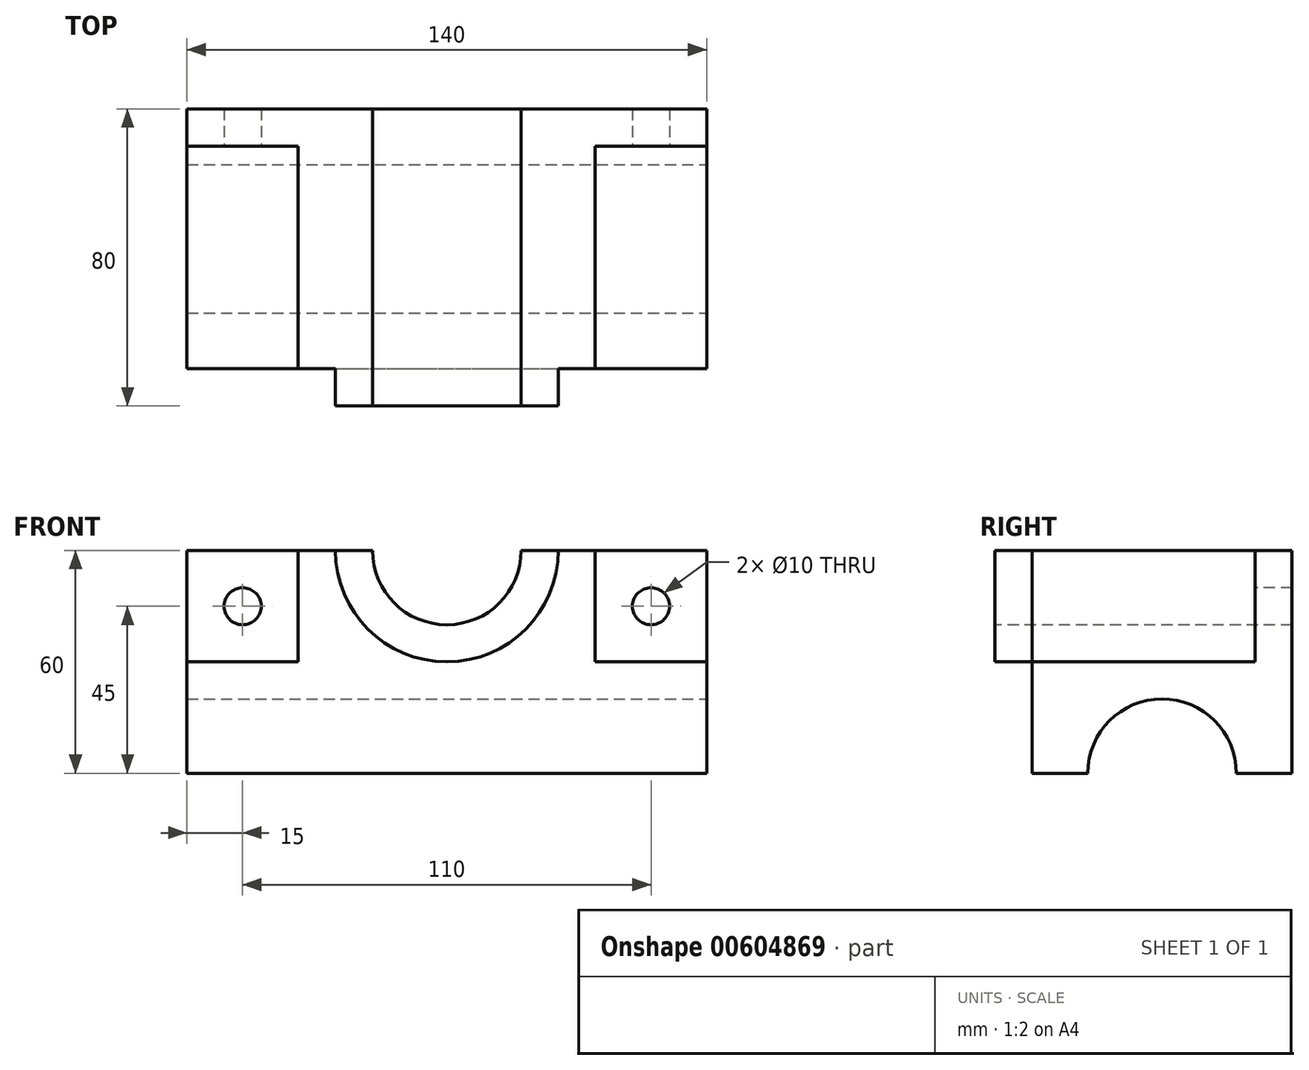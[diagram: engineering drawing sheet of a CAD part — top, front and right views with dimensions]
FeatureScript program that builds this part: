
annotation { "Feature Type Name" : "Feature", "Feature Type Description" : "" }
export const myFeature = defineFeature(function(context is Context, id is Id, definition is map)
    precondition{}
    {
        {
            var Q0;
            Q0=qCreatedBy(makeId("Top.planeOp"),FACE);
            var sketch = newSketch(context, id + "F0", { "sketchPlane" : qUnion([Q0])});
            skLineSegment(sketch, "E0.bottom", {"start": v(0, 0) * mm, "end": v(140, 0) * mm});
            skLineSegment(sketch, "E0.top", {"start": v(0, 70) * mm, "end": v(140, 70) * mm});
            skLineSegment(sketch, "E0.left", {"start": v(0, 0) * mm, "end": v(0, 70) * mm});
            skLineSegment(sketch, "E0.right", {"start": v(140, 0) * mm, "end": v(140, 70) * mm});
            skSolve(sketch);
        }
        {
            var Q0;
            Q0=makeQuery(id+"F0.imprint","IMPRINT",FACE,{"disambiguationData":[TD([[makeQuery(id+"F0.imprint","IMPRINT",EDGE,{"derivedFrom":sQuery(id+"F0.wireOp",EDGE,"E0.bottom")}),1.0]])]});
            extrude(context, id + "F1", {"entities" : qUnion([Q0]), "depth" : 60 * mm, "offsetDistance" : 25 * mm});
        }
        {
            var Q0;
            Q0=makeQuery(id+"F1.opExtrude","SWEPT_FACE",FACE,{"disambiguationData":[OSD([sQuery(id+"F0.wireOp",EDGE,"E0.bottom")])]});
            var sketch = newSketch(context, id + "F2", { "sketchPlane" : qUnion([Q0])});
            skLineSegment(sketch, "E1.bottom", {"start": v(140, 60) * mm, "end": v(110, 60) * mm});
            skLineSegment(sketch, "E1.top", {"start": v(140, 30) * mm, "end": v(110, 30) * mm});
            skLineSegment(sketch, "E1.left", {"start": v(140, 60) * mm, "end": v(140, 30) * mm});
            skLineSegment(sketch, "E1.right", {"start": v(110, 60) * mm, "end": v(110, 30) * mm});
            skLineSegment(sketch, "E2.bottom", {"start": v(0, 60) * mm, "end": v(30, 60) * mm});
            skLineSegment(sketch, "E2.top", {"start": v(0, 30) * mm, "end": v(30, 30) * mm});
            skLineSegment(sketch, "E2.left", {"start": v(0, 60) * mm, "end": v(0, 30) * mm});
            skLineSegment(sketch, "E2.right", {"start": v(30, 60) * mm, "end": v(30, 30) * mm});
            skSolve(sketch);
        }
        {
            var Q0;
            Q0=makeQuery(id+"F2.imprint","IMPRINT",FACE,{"disambiguationData":[TD([[makeQuery(id+"F2.imprint","IMPRINT",EDGE,{"derivedFrom":sQuery(id+"F2.wireOp",EDGE,"E2.bottom")}),-1.0]])]});
            extrude(context, id + "F3", {"entities" : qUnion([Q0]), "operationType" : NewBodyOperationType.REMOVE, "oppositeDirection" : true, "depth" : 60 * mm, "offsetDistance" : 25 * mm});
        }
        {
            var Q0;
            Q0=makeQuery(id+"F2.imprint","IMPRINT",FACE,{"disambiguationData":[TD([[makeQuery(id+"F2.imprint","IMPRINT",EDGE,{"derivedFrom":sQuery(id+"F2.wireOp",EDGE,"E1.bottom")}),-1.0]])]});
            extrude(context, id + "F4", {"entities" : qUnion([Q0]), "operationType" : NewBodyOperationType.REMOVE, "oppositeDirection" : true, "depth" : 60 * mm, "offsetDistance" : 25 * mm});
        }
        {
            var Q0;
            Q0=makeQuery(id+"F3.boolean.opBoolean","COPY",FACE,{"derivedFrom":makeQuery(id+"F3.opExtrude","CAP_FACE",FACE,{"disambiguationData":[OSD([sQuery(id+"F2.wireOp",EDGE,"E2.bottom"),sQuery(id+"F2.wireOp",EDGE,"E2.top"),sQuery(id+"F2.wireOp",EDGE,"E2.left"),sQuery(id+"F2.wireOp",EDGE,"E2.right")])],"isStart":false})});
            var sketch = newSketch(context, id + "F5", { "sketchPlane" : qUnion([Q0])});
            skLineSegment(sketch, "E3", {"start": v(15, 60) * mm, "end": v(15, 45) * mm, "construction": true});
            skLineSegment(sketch, "E4", {"start": v(0, 45) * mm, "end": v(15, 45) * mm, "construction": true});
            skCircle(sketch, "E5", {"center": v(15, 45) * mm, "radius": 5 * mm});
            skLineSegment(sketch, "E6", {"start": v(125, 60) * mm, "end": v(125, 45) * mm, "construction": true});
            skLineSegment(sketch, "E7", {"start": v(140, 45) * mm, "end": v(125, 45) * mm, "construction": true});
            skCircle(sketch, "E8", {"center": v(125, 45) * mm, "radius": 5 * mm});
            skSolve(sketch);
        }
        {
            var Q0;
            Q0=makeQuery(id+"F5.imprint","IMPRINT",FACE,{"disambiguationData":[TD([[makeQuery(id+"F5.imprint","IMPRINT",EDGE,{"derivedFrom":sQuery(id+"F5.wireOp",EDGE,"E5")}),1.0]])]});
            var Q1;
            Q1=makeQuery(id+"F5.imprint","IMPRINT",FACE,{"disambiguationData":[TD([[makeQuery(id+"F5.imprint","IMPRINT",EDGE,{"derivedFrom":sQuery(id+"F5.wireOp",EDGE,"E8")}),1.0]])]});
            extrude(context, id + "F6", {"entities" : qUnion([Q0, Q1]), "operationType" : NewBodyOperationType.REMOVE, "endBound" : BoundingType.UP_TO_NEXT, "oppositeDirection" : true, "depth" : 25 * mm, "offsetDistance" : 25 * mm});
        }
        {
            var Q0;
            Q0=makeQuery(id+"F1.opExtrude","SWEPT_FACE",FACE,{"disambiguationData":[OSD([sQuery(id+"F0.wireOp",EDGE,"E0.bottom")])]});
            var sketch = newSketch(context, id + "F7", { "sketchPlane" : qUnion([Q0])});
            skCircle(sketch, "E9", {"center": v(70, 60) * mm, "radius": 20 * mm});
            skCircle(sketch, "E10", {"center": v(70, 60) * mm, "radius": 30 * mm});
            skSolve(sketch);
        }
        {
            var Q0;
            {var subQ0=sQuery(id+"F7.wireOp",EDGE,"E9");var subQ1=makeQuery(id+"F1.opExtrude","CAP_EDGE",EDGE,{"disambiguationData":[OSD([sQuery(id+"F0.wireOp",EDGE,"E0.bottom")])],"isStart":false});var subQ2=makeQuery(id+"F7.imprint","INTERSECT",VERTEX,{"disambiguationData":[OD(0.0)],"derivedFrom":[subQ1,subQ0]});Q0=makeQuery(id+"F7.imprint","IMPRINT",FACE,{"disambiguationData":[TD([[makeQuery(id+"F7.imprint","IMPRINT",EDGE,{"disambiguationData":[TD([[subQ2,-1.0]])],"derivedFrom":subQ0}),1.0]])]});}
            extrude(context, id + "F8", {"entities" : qUnion([Q0]), "operationType" : NewBodyOperationType.REMOVE, "endBound" : BoundingType.UP_TO_NEXT, "oppositeDirection" : true, "depth" : 25 * mm, "offsetDistance" : 25 * mm});
        }
        {
            var Q0;
            Q0=makeQuery(id+"F1.opExtrude","SWEPT_FACE",FACE,{"disambiguationData":[OSD([sQuery(id+"F0.wireOp",EDGE,"E0.right")])]});
            var sketch = newSketch(context, id + "F9", { "sketchPlane" : qUnion([Q0])});
            skCircle(sketch, "E11", {"center": v(35, 0) * mm, "radius": 20 * mm});
            skSolve(sketch);
        }
        {
            var Q0;
            {var subQ0=sQuery(id+"F9.wireOp",EDGE,"E11");var subQ1=makeQuery(id+"F1.opExtrude","CAP_EDGE",EDGE,{"disambiguationData":[OSD([sQuery(id+"F0.wireOp",EDGE,"E0.right")])],"isStart":true});var subQ2=makeQuery(id+"F9.imprint","INTERSECT",VERTEX,{"disambiguationData":[OD(0.0)],"derivedFrom":[subQ1,subQ0]});Q0=makeQuery(id+"F9.imprint","IMPRINT",FACE,{"disambiguationData":[TD([[makeQuery(id+"F9.imprint","IMPRINT",EDGE,{"disambiguationData":[TD([[subQ2,1.0]])],"derivedFrom":subQ0}),1.0]])]});}
            extrude(context, id + "F10", {"entities" : qUnion([Q0]), "operationType" : NewBodyOperationType.REMOVE, "endBound" : BoundingType.UP_TO_NEXT, "oppositeDirection" : true, "depth" : 25 * mm, "offsetDistance" : 25 * mm});
        }
        {
            var Q0;
            {var subQ0=sQuery(id+"F7.wireOp",EDGE,"E9");var subQ1=makeQuery(id+"F1.opExtrude","CAP_EDGE",EDGE,{"disambiguationData":[OSD([sQuery(id+"F0.wireOp",EDGE,"E0.bottom")])],"isStart":false});var subQ2=makeQuery(id+"F7.imprint","INTERSECT",VERTEX,{"disambiguationData":[OD(0.0)],"derivedFrom":[subQ1,subQ0]});Q0=makeQuery(id+"F7.imprint","IMPRINT",FACE,{"disambiguationData":[TD([[makeQuery(id+"F7.imprint","IMPRINT",EDGE,{"disambiguationData":[TD([[subQ2,-1.0]])],"derivedFrom":subQ0}),-1.0]])]});}
            extrude(context, id + "F11", {"entities" : qUnion([Q0]), "operationType" : NewBodyOperationType.ADD, "depth" : 10 * mm, "offsetDistance" : 25 * mm});
        }
    });
